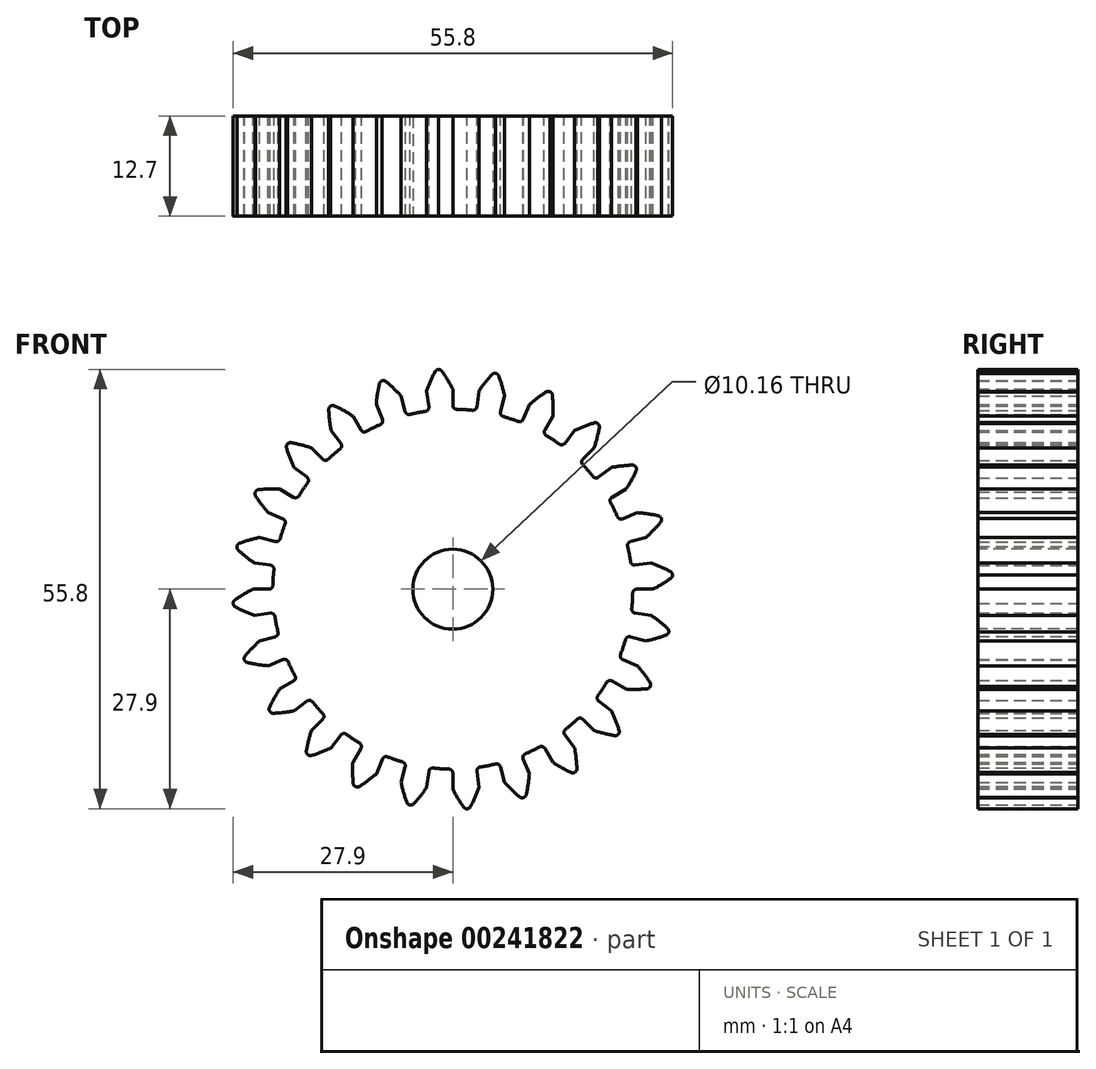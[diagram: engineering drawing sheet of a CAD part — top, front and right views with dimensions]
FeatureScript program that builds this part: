
annotation { "Feature Type Name" : "Feature", "Feature Type Description" : "" }
export const myFeature = defineFeature(function(context is Context, id is Id, definition is map)
    precondition{}
    {
        {
            var Q0;
            Q0=qCreatedBy(makeId("Front.planeOp"),FACE);
            var sketch = newSketch(context, id + "F0", { "sketchPlane" : qUnion([Q0])});
            skArc(sketch, "E0", {"start": v(-3.48, 22.6) * mm, "mid": v(1.5, -22.81) * mm, "end": v(0.5, 22.85) * mm});
            skLineSegment(sketch, "E1", {"start": v(0, 0) * mm, "end": v(-2.26, 34.54) * mm, "construction": true});
            skLineSegment(sketch, "E2", {"start": v(-1.78, 27.9) * mm, "end": v(-1.83, 27.9) * mm});
            skLineSegment(sketch, "E3", {"start": v(0, 25.4) * mm, "end": v(0, 23.36) * mm});
            skArc(sketch, "E4.trimOffspring", {"start": v(0, 25.4) * mm, "mid": v(-0.64, 26.56) * mm, "end": v(-1.37, 27.68) * mm});
            skLineSegment(sketch, "E5.MirrorCS", {"start": v(-1.87, 27.9) * mm, "end": v(-1.83, 27.9) * mm});
            skArc(sketch, "E6.MirrorCS", {"start": v(-3.32, 25.18) * mm, "mid": v(-2.83, 26.42) * mm, "end": v(-2.26, 27.62) * mm});
            skLineSegment(sketch, "E7.MirrorCS", {"start": v(-3.32, 25.18) * mm, "end": v(-3.05, 23.16) * mm});
            skPoint(sketch, "E8.visualSharp", {"position": v(-2.13, 27.86) * mm});
            skArc(sketch, "E8.filletArc", {"start": v(-1.87, 27.9) * mm, "mid": v(-2.1, 27.8) * mm, "end": v(-2.26, 27.62) * mm});
            skPoint(sketch, "E9.visualSharp", {"position": v(-1.52, 27.9) * mm});
            skArc(sketch, "E9.filletArc", {"start": v(-1.37, 27.68) * mm, "mid": v(-1.55, 27.84) * mm, "end": v(-1.78, 27.9) * mm});
            skPoint(sketch, "E10.visualSharp", {"position": v(-2.98, 22.66) * mm});
            skArc(sketch, "E10.filletArc", {"start": v(-3.48, 22.6) * mm, "mid": v(-3.15, 22.8) * mm, "end": v(-3.05, 23.16) * mm});
            skPoint(sketch, "E11.visualSharp", {"position": v(0, 22.86) * mm});
            skArc(sketch, "E11.filletArc", {"start": v(0, 23.36) * mm, "mid": v(0.14, 23) * mm, "end": v(0.5, 22.85) * mm});
            skArc(sketch, "E12.1.0", {"start": v(-9.03, 26.46) * mm, "mid": v(-9.22, 26.31) * mm, "end": v(-9.33, 26.1) * mm});
            skArc(sketch, "E12.1.1", {"start": v(-9.72, 23.47) * mm, "mid": v(-9.57, 24.79) * mm, "end": v(-9.33, 26.1) * mm});
            skLineSegment(sketch, "E12.1.2", {"start": v(-9.72, 23.47) * mm, "end": v(-8.94, 21.58) * mm});
            skArc(sketch, "E12.1.3", {"start": v(-9.2, 20.92) * mm, "mid": v(-8.94, 21.2) * mm, "end": v(-8.94, 21.58) * mm});
            skArc(sketch, "E12.1.4", {"start": v(-6.57, 24.53) * mm, "mid": v(-7.5, 25.5) * mm, "end": v(-8.49, 26.38) * mm});
            skLineSegment(sketch, "E12.1.5", {"start": v(-6.57, 24.53) * mm, "end": v(-6.05, 22.57) * mm});
            skArc(sketch, "E12.1.6", {"start": v(-6.05, 22.57) * mm, "mid": v(-5.81, 22.26) * mm, "end": v(-5.44, 22.2) * mm});
            skArc(sketch, "E12.1.7", {"start": v(-8.49, 26.38) * mm, "mid": v(-8.7, 26.5) * mm, "end": v(-8.94, 26.49) * mm});
            skLineSegment(sketch, "E12.1.8", {"start": v(-8.94, 26.49) * mm, "end": v(-8.99, 26.47) * mm});
            skLineSegment(sketch, "E12.1.9", {"start": v(-9.03, 26.46) * mm, "end": v(-8.99, 26.47) * mm});
            skArc(sketch, "E12.2.0", {"start": v(-15.57, 23.22) * mm, "mid": v(-15.72, 23.03) * mm, "end": v(-15.77, 22.8) * mm});
            skArc(sketch, "E12.2.1", {"start": v(-15.46, 20.15) * mm, "mid": v(-15.66, 21.47) * mm, "end": v(-15.77, 22.8) * mm});
            skLineSegment(sketch, "E12.2.2", {"start": v(-15.46, 20.15) * mm, "end": v(-14.22, 18.53) * mm});
            skArc(sketch, "E12.2.3", {"start": v(-14.3, 17.83) * mm, "mid": v(-14.12, 18.16) * mm, "end": v(-14.22, 18.53) * mm});
            skArc(sketch, "E12.2.4", {"start": v(-12.7, 22) * mm, "mid": v(-13.84, 22.68) * mm, "end": v(-15.03, 23.29) * mm});
            skLineSegment(sketch, "E12.2.5", {"start": v(-12.7, 22) * mm, "end": v(-11.68, 20.23) * mm});
            skArc(sketch, "E12.2.6", {"start": v(-11.68, 20.23) * mm, "mid": v(-11.38, 20) * mm, "end": v(-11, 20.04) * mm});
            skArc(sketch, "E12.2.7", {"start": v(-15.03, 23.29) * mm, "mid": v(-15.26, 23.34) * mm, "end": v(-15.5, 23.27) * mm});
            skLineSegment(sketch, "E12.2.8", {"start": v(-15.5, 23.27) * mm, "end": v(-15.53, 23.25) * mm});
            skLineSegment(sketch, "E12.2.9", {"start": v(-15.57, 23.22) * mm, "end": v(-15.53, 23.25) * mm});
            skArc(sketch, "E12.3.0", {"start": v(-21.05, 18.4) * mm, "mid": v(-21.14, 18.18) * mm, "end": v(-21.13, 17.94) * mm});
            skArc(sketch, "E12.3.1", {"start": v(-20.15, 15.46) * mm, "mid": v(-20.68, 16.68) * mm, "end": v(-21.13, 17.94) * mm});
            skLineSegment(sketch, "E12.3.2", {"start": v(-20.15, 15.46) * mm, "end": v(-18.53, 14.22) * mm});
            skArc(sketch, "E12.3.3", {"start": v(-18.43, 13.52) * mm, "mid": v(-18.34, 13.9) * mm, "end": v(-18.53, 14.22) * mm});
            skArc(sketch, "E12.3.4", {"start": v(-17.96, 17.96) * mm, "mid": v(-19.24, 18.33) * mm, "end": v(-20.54, 18.6) * mm});
            skLineSegment(sketch, "E12.3.5", {"start": v(-17.96, 17.96) * mm, "end": v(-16.52, 16.52) * mm});
            skArc(sketch, "E12.3.6", {"start": v(-16.52, 16.52) * mm, "mid": v(-16.17, 16.37) * mm, "end": v(-15.8, 16.51) * mm});
            skArc(sketch, "E12.3.7", {"start": v(-20.54, 18.6) * mm, "mid": v(-20.78, 18.6) * mm, "end": v(-20.99, 18.47) * mm});
            skLineSegment(sketch, "E12.3.8", {"start": v(-20.99, 18.47) * mm, "end": v(-21.02, 18.43) * mm});
            skLineSegment(sketch, "E12.3.9", {"start": v(-21.05, 18.4) * mm, "end": v(-21.02, 18.43) * mm});
            skArc(sketch, "E12.4.0", {"start": v(-25.1, 12.32) * mm, "mid": v(-25.13, 12.09) * mm, "end": v(-25.05, 11.86) * mm});
            skArc(sketch, "E12.4.1", {"start": v(-23.47, 9.72) * mm, "mid": v(-24.3, 10.76) * mm, "end": v(-25.05, 11.86) * mm});
            skLineSegment(sketch, "E12.4.2", {"start": v(-23.47, 9.72) * mm, "end": v(-21.58, 8.94) * mm});
            skArc(sketch, "E12.4.3", {"start": v(-21.3, 8.29) * mm, "mid": v(-21.31, 8.67) * mm, "end": v(-21.58, 8.94) * mm});
            skArc(sketch, "E12.4.4", {"start": v(-22, 12.7) * mm, "mid": v(-23.33, 12.72) * mm, "end": v(-24.66, 12.66) * mm});
            skLineSegment(sketch, "E12.4.5", {"start": v(-22, 12.7) * mm, "end": v(-20.23, 11.68) * mm});
            skArc(sketch, "E12.4.6", {"start": v(-20.23, 11.68) * mm, "mid": v(-19.85, 11.63) * mm, "end": v(-19.54, 11.86) * mm});
            skArc(sketch, "E12.4.7", {"start": v(-24.66, 12.66) * mm, "mid": v(-24.89, 12.58) * mm, "end": v(-25.05, 12.4) * mm});
            skLineSegment(sketch, "E12.4.8", {"start": v(-25.05, 12.4) * mm, "end": v(-25.08, 12.37) * mm});
            skLineSegment(sketch, "E12.4.9", {"start": v(-25.1, 12.32) * mm, "end": v(-25.08, 12.37) * mm});
            skArc(sketch, "E12.5.0", {"start": v(-27.43, 5.41) * mm, "mid": v(-27.4, 5.17) * mm, "end": v(-27.27, 4.97) * mm});
            skArc(sketch, "E12.5.1", {"start": v(-25.18, 3.32) * mm, "mid": v(-26.25, 4.1) * mm, "end": v(-27.27, 4.97) * mm});
            skLineSegment(sketch, "E12.5.2", {"start": v(-25.18, 3.32) * mm, "end": v(-23.16, 3.05) * mm});
            skArc(sketch, "E12.5.3", {"start": v(-22.72, 2.5) * mm, "mid": v(-22.83, 2.86) * mm, "end": v(-23.16, 3.05) * mm});
            skArc(sketch, "E12.5.4", {"start": v(-24.53, 6.57) * mm, "mid": v(-25.83, 6.25) * mm, "end": v(-27.1, 5.84) * mm});
            skLineSegment(sketch, "E12.5.5", {"start": v(-24.53, 6.57) * mm, "end": v(-22.57, 6.05) * mm});
            skArc(sketch, "E12.5.6", {"start": v(-22.57, 6.05) * mm, "mid": v(-22.19, 6.1) * mm, "end": v(-21.95, 6.4) * mm});
            skArc(sketch, "E12.5.7", {"start": v(-27.1, 5.84) * mm, "mid": v(-27.3, 5.7) * mm, "end": v(-27.4, 5.5) * mm});
            skLineSegment(sketch, "E12.5.8", {"start": v(-27.4, 5.5) * mm, "end": v(-27.42, 5.45) * mm});
            skLineSegment(sketch, "E12.5.9", {"start": v(-27.43, 5.41) * mm, "end": v(-27.42, 5.45) * mm});
            skArc(sketch, "E12.6.0", {"start": v(-27.9, -1.87) * mm, "mid": v(-27.8, -2.1) * mm, "end": v(-27.62, -2.26) * mm});
            skArc(sketch, "E12.6.1", {"start": v(-25.18, -3.32) * mm, "mid": v(-26.42, -2.83) * mm, "end": v(-27.62, -2.26) * mm});
            skLineSegment(sketch, "E12.6.2", {"start": v(-25.18, -3.32) * mm, "end": v(-23.16, -3.05) * mm});
            skArc(sketch, "E12.6.3", {"start": v(-22.6, -3.48) * mm, "mid": v(-22.8, -3.15) * mm, "end": v(-23.16, -3.05) * mm});
            skArc(sketch, "E12.6.4", {"start": v(-25.4, 0) * mm, "mid": v(-26.56, -0.64) * mm, "end": v(-27.68, -1.37) * mm});
            skLineSegment(sketch, "E12.6.5", {"start": v(-25.4, 0) * mm, "end": v(-23.36, 0) * mm});
            skArc(sketch, "E12.6.6", {"start": v(-23.36, 0) * mm, "mid": v(-23, 0.14) * mm, "end": v(-22.85, 0.5) * mm});
            skArc(sketch, "E12.6.7", {"start": v(-27.68, -1.37) * mm, "mid": v(-27.84, -1.55) * mm, "end": v(-27.9, -1.78) * mm});
            skLineSegment(sketch, "E12.6.8", {"start": v(-27.9, -1.78) * mm, "end": v(-27.9, -1.83) * mm});
            skLineSegment(sketch, "E12.6.9", {"start": v(-27.9, -1.87) * mm, "end": v(-27.9, -1.83) * mm});
            skArc(sketch, "E12.7.0", {"start": v(-26.46, -9.03) * mm, "mid": v(-26.31, -9.22) * mm, "end": v(-26.1, -9.33) * mm});
            skArc(sketch, "E12.7.1", {"start": v(-23.47, -9.72) * mm, "mid": v(-24.79, -9.57) * mm, "end": v(-26.1, -9.33) * mm});
            skLineSegment(sketch, "E12.7.2", {"start": v(-23.47, -9.72) * mm, "end": v(-21.58, -8.94) * mm});
            skArc(sketch, "E12.7.3", {"start": v(-20.92, -9.2) * mm, "mid": v(-21.2, -8.94) * mm, "end": v(-21.58, -8.94) * mm});
            skArc(sketch, "E12.7.4", {"start": v(-24.53, -6.57) * mm, "mid": v(-25.5, -7.5) * mm, "end": v(-26.38, -8.49) * mm});
            skLineSegment(sketch, "E12.7.5", {"start": v(-24.53, -6.57) * mm, "end": v(-22.57, -6.05) * mm});
            skArc(sketch, "E12.7.6", {"start": v(-22.57, -6.05) * mm, "mid": v(-22.26, -5.81) * mm, "end": v(-22.2, -5.44) * mm});
            skArc(sketch, "E12.7.7", {"start": v(-26.38, -8.49) * mm, "mid": v(-26.5, -8.7) * mm, "end": v(-26.49, -8.94) * mm});
            skLineSegment(sketch, "E12.7.8", {"start": v(-26.49, -8.94) * mm, "end": v(-26.47, -8.99) * mm});
            skLineSegment(sketch, "E12.7.9", {"start": v(-26.46, -9.03) * mm, "end": v(-26.47, -8.99) * mm});
            skArc(sketch, "E12.8.0", {"start": v(-23.22, -15.57) * mm, "mid": v(-23.03, -15.72) * mm, "end": v(-22.8, -15.77) * mm});
            skArc(sketch, "E12.8.1", {"start": v(-20.15, -15.46) * mm, "mid": v(-21.47, -15.66) * mm, "end": v(-22.8, -15.77) * mm});
            skLineSegment(sketch, "E12.8.2", {"start": v(-20.15, -15.46) * mm, "end": v(-18.53, -14.22) * mm});
            skArc(sketch, "E12.8.3", {"start": v(-17.83, -14.3) * mm, "mid": v(-18.16, -14.12) * mm, "end": v(-18.53, -14.22) * mm});
            skArc(sketch, "E12.8.4", {"start": v(-22, -12.7) * mm, "mid": v(-22.68, -13.84) * mm, "end": v(-23.29, -15.03) * mm});
            skLineSegment(sketch, "E12.8.5", {"start": v(-22, -12.7) * mm, "end": v(-20.23, -11.68) * mm});
            skArc(sketch, "E12.8.6", {"start": v(-20.23, -11.68) * mm, "mid": v(-20, -11.38) * mm, "end": v(-20.04, -11) * mm});
            skArc(sketch, "E12.8.7", {"start": v(-23.29, -15.03) * mm, "mid": v(-23.34, -15.26) * mm, "end": v(-23.27, -15.5) * mm});
            skLineSegment(sketch, "E12.8.8", {"start": v(-23.27, -15.5) * mm, "end": v(-23.25, -15.53) * mm});
            skLineSegment(sketch, "E12.8.9", {"start": v(-23.22, -15.57) * mm, "end": v(-23.25, -15.53) * mm});
            skArc(sketch, "E12.9.0", {"start": v(-18.4, -21.05) * mm, "mid": v(-18.18, -21.14) * mm, "end": v(-17.94, -21.13) * mm});
            skArc(sketch, "E12.9.1", {"start": v(-15.46, -20.15) * mm, "mid": v(-16.68, -20.68) * mm, "end": v(-17.94, -21.13) * mm});
            skLineSegment(sketch, "E12.9.2", {"start": v(-15.46, -20.15) * mm, "end": v(-14.22, -18.53) * mm});
            skArc(sketch, "E12.9.3", {"start": v(-13.52, -18.43) * mm, "mid": v(-13.9, -18.34) * mm, "end": v(-14.22, -18.53) * mm});
            skArc(sketch, "E12.9.4", {"start": v(-17.96, -17.96) * mm, "mid": v(-18.33, -19.24) * mm, "end": v(-18.6, -20.54) * mm});
            skLineSegment(sketch, "E12.9.5", {"start": v(-17.96, -17.96) * mm, "end": v(-16.52, -16.52) * mm});
            skArc(sketch, "E12.9.6", {"start": v(-16.52, -16.52) * mm, "mid": v(-16.37, -16.17) * mm, "end": v(-16.51, -15.8) * mm});
            skArc(sketch, "E12.9.7", {"start": v(-18.6, -20.54) * mm, "mid": v(-18.6, -20.78) * mm, "end": v(-18.47, -20.99) * mm});
            skLineSegment(sketch, "E12.9.8", {"start": v(-18.47, -20.99) * mm, "end": v(-18.43, -21.02) * mm});
            skLineSegment(sketch, "E12.9.9", {"start": v(-18.4, -21.05) * mm, "end": v(-18.43, -21.02) * mm});
            skArc(sketch, "E12.10.0", {"start": v(-12.32, -25.1) * mm, "mid": v(-12.09, -25.13) * mm, "end": v(-11.86, -25.05) * mm});
            skArc(sketch, "E12.10.1", {"start": v(-9.72, -23.47) * mm, "mid": v(-10.76, -24.3) * mm, "end": v(-11.86, -25.05) * mm});
            skLineSegment(sketch, "E12.10.2", {"start": v(-9.72, -23.47) * mm, "end": v(-8.94, -21.58) * mm});
            skArc(sketch, "E12.10.3", {"start": v(-8.29, -21.3) * mm, "mid": v(-8.67, -21.31) * mm, "end": v(-8.94, -21.58) * mm});
            skArc(sketch, "E12.10.4", {"start": v(-12.7, -22) * mm, "mid": v(-12.72, -23.33) * mm, "end": v(-12.66, -24.66) * mm});
            skLineSegment(sketch, "E12.10.5", {"start": v(-12.7, -22) * mm, "end": v(-11.68, -20.23) * mm});
            skArc(sketch, "E12.10.6", {"start": v(-11.68, -20.23) * mm, "mid": v(-11.63, -19.85) * mm, "end": v(-11.86, -19.54) * mm});
            skArc(sketch, "E12.10.7", {"start": v(-12.66, -24.66) * mm, "mid": v(-12.58, -24.89) * mm, "end": v(-12.4, -25.05) * mm});
            skLineSegment(sketch, "E12.10.8", {"start": v(-12.4, -25.05) * mm, "end": v(-12.37, -25.08) * mm});
            skLineSegment(sketch, "E12.10.9", {"start": v(-12.32, -25.1) * mm, "end": v(-12.37, -25.08) * mm});
            skArc(sketch, "E12.11.0", {"start": v(-5.41, -27.43) * mm, "mid": v(-5.17, -27.4) * mm, "end": v(-4.97, -27.27) * mm});
            skArc(sketch, "E12.11.1", {"start": v(-3.32, -25.18) * mm, "mid": v(-4.1, -26.25) * mm, "end": v(-4.97, -27.27) * mm});
            skLineSegment(sketch, "E12.11.2", {"start": v(-3.32, -25.18) * mm, "end": v(-3.05, -23.16) * mm});
            skArc(sketch, "E12.11.3", {"start": v(-2.5, -22.72) * mm, "mid": v(-2.86, -22.83) * mm, "end": v(-3.05, -23.16) * mm});
            skArc(sketch, "E12.11.4", {"start": v(-6.57, -24.53) * mm, "mid": v(-6.25, -25.83) * mm, "end": v(-5.84, -27.1) * mm});
            skLineSegment(sketch, "E12.11.5", {"start": v(-6.57, -24.53) * mm, "end": v(-6.05, -22.57) * mm});
            skArc(sketch, "E12.11.6", {"start": v(-6.05, -22.57) * mm, "mid": v(-6.1, -22.19) * mm, "end": v(-6.4, -21.95) * mm});
            skArc(sketch, "E12.11.7", {"start": v(-5.84, -27.1) * mm, "mid": v(-5.7, -27.3) * mm, "end": v(-5.5, -27.4) * mm});
            skLineSegment(sketch, "E12.11.8", {"start": v(-5.5, -27.4) * mm, "end": v(-5.45, -27.42) * mm});
            skLineSegment(sketch, "E12.11.9", {"start": v(-5.41, -27.43) * mm, "end": v(-5.45, -27.42) * mm});
            skArc(sketch, "E12.12.0", {"start": v(1.87, -27.9) * mm, "mid": v(2.1, -27.8) * mm, "end": v(2.26, -27.62) * mm});
            skArc(sketch, "E12.12.1", {"start": v(3.32, -25.18) * mm, "mid": v(2.83, -26.42) * mm, "end": v(2.26, -27.62) * mm});
            skLineSegment(sketch, "E12.12.2", {"start": v(3.32, -25.18) * mm, "end": v(3.05, -23.16) * mm});
            skArc(sketch, "E12.12.3", {"start": v(3.48, -22.6) * mm, "mid": v(3.15, -22.8) * mm, "end": v(3.05, -23.16) * mm});
            skArc(sketch, "E12.12.4", {"start": v(0, -25.4) * mm, "mid": v(0.64, -26.56) * mm, "end": v(1.37, -27.68) * mm});
            skLineSegment(sketch, "E12.12.5", {"start": v(0, -25.4) * mm, "end": v(0, -23.36) * mm});
            skArc(sketch, "E12.12.6", {"start": v(0, -23.36) * mm, "mid": v(-0.14, -23) * mm, "end": v(-0.5, -22.85) * mm});
            skArc(sketch, "E12.12.7", {"start": v(1.37, -27.68) * mm, "mid": v(1.55, -27.84) * mm, "end": v(1.78, -27.9) * mm});
            skLineSegment(sketch, "E12.12.8", {"start": v(1.78, -27.9) * mm, "end": v(1.83, -27.9) * mm});
            skLineSegment(sketch, "E12.12.9", {"start": v(1.87, -27.9) * mm, "end": v(1.83, -27.9) * mm});
            skArc(sketch, "E12.13.0", {"start": v(9.03, -26.46) * mm, "mid": v(9.22, -26.31) * mm, "end": v(9.33, -26.1) * mm});
            skArc(sketch, "E12.13.1", {"start": v(9.72, -23.47) * mm, "mid": v(9.57, -24.79) * mm, "end": v(9.33, -26.1) * mm});
            skLineSegment(sketch, "E12.13.2", {"start": v(9.72, -23.47) * mm, "end": v(8.94, -21.58) * mm});
            skArc(sketch, "E12.13.3", {"start": v(9.2, -20.92) * mm, "mid": v(8.94, -21.2) * mm, "end": v(8.94, -21.58) * mm});
            skArc(sketch, "E12.13.4", {"start": v(6.57, -24.53) * mm, "mid": v(7.5, -25.5) * mm, "end": v(8.49, -26.38) * mm});
            skLineSegment(sketch, "E12.13.5", {"start": v(6.57, -24.53) * mm, "end": v(6.05, -22.57) * mm});
            skArc(sketch, "E12.13.6", {"start": v(6.05, -22.57) * mm, "mid": v(5.81, -22.26) * mm, "end": v(5.44, -22.2) * mm});
            skArc(sketch, "E12.13.7", {"start": v(8.49, -26.38) * mm, "mid": v(8.7, -26.5) * mm, "end": v(8.94, -26.49) * mm});
            skLineSegment(sketch, "E12.13.8", {"start": v(8.94, -26.49) * mm, "end": v(8.99, -26.47) * mm});
            skLineSegment(sketch, "E12.13.9", {"start": v(9.03, -26.46) * mm, "end": v(8.99, -26.47) * mm});
            skArc(sketch, "E12.14.0", {"start": v(15.57, -23.22) * mm, "mid": v(15.72, -23.03) * mm, "end": v(15.77, -22.8) * mm});
            skArc(sketch, "E12.14.1", {"start": v(15.46, -20.15) * mm, "mid": v(15.66, -21.47) * mm, "end": v(15.77, -22.8) * mm});
            skLineSegment(sketch, "E12.14.2", {"start": v(15.46, -20.15) * mm, "end": v(14.22, -18.53) * mm});
            skArc(sketch, "E12.14.3", {"start": v(14.3, -17.83) * mm, "mid": v(14.12, -18.16) * mm, "end": v(14.22, -18.53) * mm});
            skArc(sketch, "E12.14.4", {"start": v(12.7, -22) * mm, "mid": v(13.84, -22.68) * mm, "end": v(15.03, -23.29) * mm});
            skLineSegment(sketch, "E12.14.5", {"start": v(12.7, -22) * mm, "end": v(11.68, -20.23) * mm});
            skArc(sketch, "E12.14.6", {"start": v(11.68, -20.23) * mm, "mid": v(11.38, -20) * mm, "end": v(11, -20.04) * mm});
            skArc(sketch, "E12.14.7", {"start": v(15.03, -23.29) * mm, "mid": v(15.26, -23.34) * mm, "end": v(15.5, -23.27) * mm});
            skLineSegment(sketch, "E12.14.8", {"start": v(15.5, -23.27) * mm, "end": v(15.53, -23.25) * mm});
            skLineSegment(sketch, "E12.14.9", {"start": v(15.57, -23.22) * mm, "end": v(15.53, -23.25) * mm});
            skArc(sketch, "E12.15.0", {"start": v(21.05, -18.4) * mm, "mid": v(21.14, -18.18) * mm, "end": v(21.13, -17.94) * mm});
            skArc(sketch, "E12.15.1", {"start": v(20.15, -15.46) * mm, "mid": v(20.68, -16.68) * mm, "end": v(21.13, -17.94) * mm});
            skLineSegment(sketch, "E12.15.2", {"start": v(20.15, -15.46) * mm, "end": v(18.53, -14.22) * mm});
            skArc(sketch, "E12.15.3", {"start": v(18.43, -13.52) * mm, "mid": v(18.34, -13.9) * mm, "end": v(18.53, -14.22) * mm});
            skArc(sketch, "E12.15.4", {"start": v(17.96, -17.96) * mm, "mid": v(19.24, -18.33) * mm, "end": v(20.54, -18.6) * mm});
            skLineSegment(sketch, "E12.15.5", {"start": v(17.96, -17.96) * mm, "end": v(16.52, -16.52) * mm});
            skArc(sketch, "E12.15.6", {"start": v(16.52, -16.52) * mm, "mid": v(16.17, -16.37) * mm, "end": v(15.8, -16.51) * mm});
            skArc(sketch, "E12.15.7", {"start": v(20.54, -18.6) * mm, "mid": v(20.78, -18.6) * mm, "end": v(20.99, -18.47) * mm});
            skLineSegment(sketch, "E12.15.8", {"start": v(20.99, -18.47) * mm, "end": v(21.02, -18.43) * mm});
            skLineSegment(sketch, "E12.15.9", {"start": v(21.05, -18.4) * mm, "end": v(21.02, -18.43) * mm});
            skArc(sketch, "E12.16.0", {"start": v(25.1, -12.32) * mm, "mid": v(25.13, -12.09) * mm, "end": v(25.05, -11.86) * mm});
            skArc(sketch, "E12.16.1", {"start": v(23.47, -9.72) * mm, "mid": v(24.3, -10.76) * mm, "end": v(25.05, -11.86) * mm});
            skLineSegment(sketch, "E12.16.2", {"start": v(23.47, -9.72) * mm, "end": v(21.58, -8.94) * mm});
            skArc(sketch, "E12.16.3", {"start": v(21.3, -8.29) * mm, "mid": v(21.31, -8.67) * mm, "end": v(21.58, -8.94) * mm});
            skArc(sketch, "E12.16.4", {"start": v(22, -12.7) * mm, "mid": v(23.33, -12.72) * mm, "end": v(24.66, -12.66) * mm});
            skLineSegment(sketch, "E12.16.5", {"start": v(22, -12.7) * mm, "end": v(20.23, -11.68) * mm});
            skArc(sketch, "E12.16.6", {"start": v(20.23, -11.68) * mm, "mid": v(19.85, -11.63) * mm, "end": v(19.54, -11.86) * mm});
            skArc(sketch, "E12.16.7", {"start": v(24.66, -12.66) * mm, "mid": v(24.89, -12.58) * mm, "end": v(25.05, -12.4) * mm});
            skLineSegment(sketch, "E12.16.8", {"start": v(25.05, -12.4) * mm, "end": v(25.08, -12.37) * mm});
            skLineSegment(sketch, "E12.16.9", {"start": v(25.1, -12.32) * mm, "end": v(25.08, -12.37) * mm});
            skArc(sketch, "E12.17.0", {"start": v(27.43, -5.41) * mm, "mid": v(27.4, -5.17) * mm, "end": v(27.27, -4.97) * mm});
            skArc(sketch, "E12.17.1", {"start": v(25.18, -3.32) * mm, "mid": v(26.25, -4.1) * mm, "end": v(27.27, -4.97) * mm});
            skLineSegment(sketch, "E12.17.2", {"start": v(25.18, -3.32) * mm, "end": v(23.16, -3.05) * mm});
            skArc(sketch, "E12.17.3", {"start": v(22.72, -2.5) * mm, "mid": v(22.83, -2.86) * mm, "end": v(23.16, -3.05) * mm});
            skArc(sketch, "E12.17.4", {"start": v(24.53, -6.57) * mm, "mid": v(25.83, -6.25) * mm, "end": v(27.1, -5.84) * mm});
            skLineSegment(sketch, "E12.17.5", {"start": v(24.53, -6.57) * mm, "end": v(22.57, -6.05) * mm});
            skArc(sketch, "E12.17.6", {"start": v(22.57, -6.05) * mm, "mid": v(22.19, -6.1) * mm, "end": v(21.95, -6.4) * mm});
            skArc(sketch, "E12.17.7", {"start": v(27.1, -5.84) * mm, "mid": v(27.3, -5.7) * mm, "end": v(27.4, -5.5) * mm});
            skLineSegment(sketch, "E12.17.8", {"start": v(27.4, -5.5) * mm, "end": v(27.42, -5.45) * mm});
            skLineSegment(sketch, "E12.17.9", {"start": v(27.43, -5.41) * mm, "end": v(27.42, -5.45) * mm});
            skArc(sketch, "E12.18.0", {"start": v(27.9, 1.87) * mm, "mid": v(27.8, 2.1) * mm, "end": v(27.62, 2.26) * mm});
            skArc(sketch, "E12.18.1", {"start": v(25.18, 3.32) * mm, "mid": v(26.42, 2.83) * mm, "end": v(27.62, 2.26) * mm});
            skLineSegment(sketch, "E12.18.2", {"start": v(25.18, 3.32) * mm, "end": v(23.16, 3.05) * mm});
            skArc(sketch, "E12.18.3", {"start": v(22.6, 3.48) * mm, "mid": v(22.8, 3.15) * mm, "end": v(23.16, 3.05) * mm});
            skArc(sketch, "E12.18.4", {"start": v(25.4, 0) * mm, "mid": v(26.56, 0.64) * mm, "end": v(27.68, 1.37) * mm});
            skLineSegment(sketch, "E12.18.5", {"start": v(25.4, 0) * mm, "end": v(23.36, 0) * mm});
            skArc(sketch, "E12.18.6", {"start": v(23.36, 0) * mm, "mid": v(23, -0.14) * mm, "end": v(22.85, -0.5) * mm});
            skArc(sketch, "E12.18.7", {"start": v(27.68, 1.37) * mm, "mid": v(27.84, 1.55) * mm, "end": v(27.9, 1.78) * mm});
            skLineSegment(sketch, "E12.18.8", {"start": v(27.9, 1.78) * mm, "end": v(27.9, 1.83) * mm});
            skLineSegment(sketch, "E12.18.9", {"start": v(27.9, 1.87) * mm, "end": v(27.9, 1.83) * mm});
            skArc(sketch, "E12.19.0", {"start": v(26.46, 9.03) * mm, "mid": v(26.31, 9.22) * mm, "end": v(26.1, 9.33) * mm});
            skArc(sketch, "E12.19.1", {"start": v(23.47, 9.72) * mm, "mid": v(24.79, 9.57) * mm, "end": v(26.1, 9.33) * mm});
            skLineSegment(sketch, "E12.19.2", {"start": v(23.47, 9.72) * mm, "end": v(21.58, 8.94) * mm});
            skArc(sketch, "E12.19.3", {"start": v(20.92, 9.2) * mm, "mid": v(21.2, 8.94) * mm, "end": v(21.58, 8.94) * mm});
            skArc(sketch, "E12.19.4", {"start": v(24.53, 6.57) * mm, "mid": v(25.5, 7.5) * mm, "end": v(26.38, 8.49) * mm});
            skLineSegment(sketch, "E12.19.5", {"start": v(24.53, 6.57) * mm, "end": v(22.57, 6.05) * mm});
            skArc(sketch, "E12.19.6", {"start": v(22.57, 6.05) * mm, "mid": v(22.26, 5.81) * mm, "end": v(22.2, 5.44) * mm});
            skArc(sketch, "E12.19.7", {"start": v(26.38, 8.49) * mm, "mid": v(26.5, 8.7) * mm, "end": v(26.49, 8.94) * mm});
            skLineSegment(sketch, "E12.19.8", {"start": v(26.49, 8.94) * mm, "end": v(26.47, 8.99) * mm});
            skLineSegment(sketch, "E12.19.9", {"start": v(26.46, 9.03) * mm, "end": v(26.47, 8.99) * mm});
            skArc(sketch, "E12.20.0", {"start": v(23.22, 15.57) * mm, "mid": v(23.03, 15.72) * mm, "end": v(22.8, 15.77) * mm});
            skArc(sketch, "E12.20.1", {"start": v(20.15, 15.46) * mm, "mid": v(21.47, 15.66) * mm, "end": v(22.8, 15.77) * mm});
            skLineSegment(sketch, "E12.20.2", {"start": v(20.15, 15.46) * mm, "end": v(18.53, 14.22) * mm});
            skArc(sketch, "E12.20.3", {"start": v(17.83, 14.3) * mm, "mid": v(18.16, 14.12) * mm, "end": v(18.53, 14.22) * mm});
            skArc(sketch, "E12.20.4", {"start": v(22, 12.7) * mm, "mid": v(22.68, 13.84) * mm, "end": v(23.29, 15.03) * mm});
            skLineSegment(sketch, "E12.20.5", {"start": v(22, 12.7) * mm, "end": v(20.23, 11.68) * mm});
            skArc(sketch, "E12.20.6", {"start": v(20.23, 11.68) * mm, "mid": v(20, 11.38) * mm, "end": v(20.04, 11) * mm});
            skArc(sketch, "E12.20.7", {"start": v(23.29, 15.03) * mm, "mid": v(23.34, 15.26) * mm, "end": v(23.27, 15.5) * mm});
            skLineSegment(sketch, "E12.20.8", {"start": v(23.27, 15.5) * mm, "end": v(23.25, 15.53) * mm});
            skLineSegment(sketch, "E12.20.9", {"start": v(23.22, 15.57) * mm, "end": v(23.25, 15.53) * mm});
            skArc(sketch, "E12.21.0", {"start": v(18.4, 21.05) * mm, "mid": v(18.18, 21.14) * mm, "end": v(17.94, 21.13) * mm});
            skArc(sketch, "E12.21.1", {"start": v(15.46, 20.15) * mm, "mid": v(16.68, 20.68) * mm, "end": v(17.94, 21.13) * mm});
            skLineSegment(sketch, "E12.21.2", {"start": v(15.46, 20.15) * mm, "end": v(14.22, 18.53) * mm});
            skArc(sketch, "E12.21.3", {"start": v(13.52, 18.43) * mm, "mid": v(13.9, 18.34) * mm, "end": v(14.22, 18.53) * mm});
            skArc(sketch, "E12.21.4", {"start": v(17.96, 17.96) * mm, "mid": v(18.33, 19.24) * mm, "end": v(18.6, 20.54) * mm});
            skLineSegment(sketch, "E12.21.5", {"start": v(17.96, 17.96) * mm, "end": v(16.52, 16.52) * mm});
            skArc(sketch, "E12.21.6", {"start": v(16.52, 16.52) * mm, "mid": v(16.37, 16.17) * mm, "end": v(16.51, 15.8) * mm});
            skArc(sketch, "E12.21.7", {"start": v(18.6, 20.54) * mm, "mid": v(18.6, 20.78) * mm, "end": v(18.47, 20.99) * mm});
            skLineSegment(sketch, "E12.21.8", {"start": v(18.47, 20.99) * mm, "end": v(18.43, 21.02) * mm});
            skLineSegment(sketch, "E12.21.9", {"start": v(18.4, 21.05) * mm, "end": v(18.43, 21.02) * mm});
            skArc(sketch, "E12.22.0", {"start": v(12.32, 25.1) * mm, "mid": v(12.09, 25.13) * mm, "end": v(11.86, 25.05) * mm});
            skArc(sketch, "E12.22.1", {"start": v(9.72, 23.47) * mm, "mid": v(10.76, 24.3) * mm, "end": v(11.86, 25.05) * mm});
            skLineSegment(sketch, "E12.22.2", {"start": v(9.72, 23.47) * mm, "end": v(8.94, 21.58) * mm});
            skArc(sketch, "E12.22.3", {"start": v(8.29, 21.3) * mm, "mid": v(8.67, 21.31) * mm, "end": v(8.94, 21.58) * mm});
            skArc(sketch, "E12.22.4", {"start": v(12.7, 22) * mm, "mid": v(12.72, 23.33) * mm, "end": v(12.66, 24.66) * mm});
            skLineSegment(sketch, "E12.22.5", {"start": v(12.7, 22) * mm, "end": v(11.68, 20.23) * mm});
            skArc(sketch, "E12.22.6", {"start": v(11.68, 20.23) * mm, "mid": v(11.63, 19.85) * mm, "end": v(11.86, 19.54) * mm});
            skArc(sketch, "E12.22.7", {"start": v(12.66, 24.66) * mm, "mid": v(12.58, 24.89) * mm, "end": v(12.4, 25.05) * mm});
            skLineSegment(sketch, "E12.22.8", {"start": v(12.4, 25.05) * mm, "end": v(12.37, 25.08) * mm});
            skLineSegment(sketch, "E12.22.9", {"start": v(12.32, 25.1) * mm, "end": v(12.37, 25.08) * mm});
            skArc(sketch, "E12.23.0", {"start": v(5.41, 27.43) * mm, "mid": v(5.17, 27.4) * mm, "end": v(4.97, 27.27) * mm});
            skArc(sketch, "E12.23.1", {"start": v(3.32, 25.18) * mm, "mid": v(4.1, 26.25) * mm, "end": v(4.97, 27.27) * mm});
            skLineSegment(sketch, "E12.23.2", {"start": v(3.32, 25.18) * mm, "end": v(3.05, 23.16) * mm});
            skArc(sketch, "E12.23.3", {"start": v(2.5, 22.72) * mm, "mid": v(2.86, 22.83) * mm, "end": v(3.05, 23.16) * mm});
            skArc(sketch, "E12.23.4", {"start": v(6.57, 24.53) * mm, "mid": v(6.25, 25.83) * mm, "end": v(5.84, 27.1) * mm});
            skLineSegment(sketch, "E12.23.5", {"start": v(6.57, 24.53) * mm, "end": v(6.05, 22.57) * mm});
            skArc(sketch, "E12.23.6", {"start": v(6.05, 22.57) * mm, "mid": v(6.1, 22.19) * mm, "end": v(6.4, 21.95) * mm});
            skArc(sketch, "E12.23.7", {"start": v(5.84, 27.1) * mm, "mid": v(5.7, 27.3) * mm, "end": v(5.5, 27.4) * mm});
            skLineSegment(sketch, "E12.23.8", {"start": v(5.5, 27.4) * mm, "end": v(5.45, 27.42) * mm});
            skLineSegment(sketch, "E12.23.9", {"start": v(5.41, 27.43) * mm, "end": v(5.45, 27.42) * mm});
            skSolve(sketch);
        }
        {
            var Q0;
            Q0 = qSketchRegion(id + "F0", true);
            extrude(context, id + "F1", {"entities" : qUnion([Q0]), "depth" : 12.7 * mm});
        }
        {
            var Q0;
            Q0=makeQuery(id+"F1.opExtrude","CAP_FACE",FACE,{"disambiguationData":[OSD([sQuery(id+"F0.wireOp",EDGE,"E0"),sQuery(id+"F0.wireOp",EDGE,"E2"),sQuery(id+"F0.wireOp",EDGE,"E3"),sQuery(id+"F0.wireOp",EDGE,"E4.trimOffspring"),sQuery(id+"F0.wireOp",EDGE,"E5.MirrorCS"),sQuery(id+"F0.wireOp",EDGE,"E6.MirrorCS"),sQuery(id+"F0.wireOp",EDGE,"E7.MirrorCS"),sQuery(id+"F0.wireOp",EDGE,"E8.filletArc"),sQuery(id+"F0.wireOp",EDGE,"E9.filletArc"),sQuery(id+"F0.wireOp",EDGE,"E10.filletArc"),sQuery(id+"F0.wireOp",EDGE,"E11.filletArc"),sQuery(id+"F0.wireOp",EDGE,"E12.1.0"),sQuery(id+"F0.wireOp",EDGE,"E12.1.1"),sQuery(id+"F0.wireOp",EDGE,"E12.1.2"),sQuery(id+"F0.wireOp",EDGE,"E12.1.3"),sQuery(id+"F0.wireOp",EDGE,"E12.1.4"),sQuery(id+"F0.wireOp",EDGE,"E12.1.5"),sQuery(id+"F0.wireOp",EDGE,"E12.1.6"),sQuery(id+"F0.wireOp",EDGE,"E12.1.7"),sQuery(id+"F0.wireOp",EDGE,"E12.1.8"),sQuery(id+"F0.wireOp",EDGE,"E12.1.9"),sQuery(id+"F0.wireOp",EDGE,"E12.2.0"),sQuery(id+"F0.wireOp",EDGE,"E12.2.1"),sQuery(id+"F0.wireOp",EDGE,"E12.2.2"),sQuery(id+"F0.wireOp",EDGE,"E12.2.3"),sQuery(id+"F0.wireOp",EDGE,"E12.2.4"),sQuery(id+"F0.wireOp",EDGE,"E12.2.5"),sQuery(id+"F0.wireOp",EDGE,"E12.2.6"),sQuery(id+"F0.wireOp",EDGE,"E12.2.7"),sQuery(id+"F0.wireOp",EDGE,"E12.2.8"),sQuery(id+"F0.wireOp",EDGE,"E12.2.9"),sQuery(id+"F0.wireOp",EDGE,"E12.3.0"),sQuery(id+"F0.wireOp",EDGE,"E12.3.1"),sQuery(id+"F0.wireOp",EDGE,"E12.3.2"),sQuery(id+"F0.wireOp",EDGE,"E12.3.3"),sQuery(id+"F0.wireOp",EDGE,"E12.3.4"),sQuery(id+"F0.wireOp",EDGE,"E12.3.5"),sQuery(id+"F0.wireOp",EDGE,"E12.3.6"),sQuery(id+"F0.wireOp",EDGE,"E12.3.7"),sQuery(id+"F0.wireOp",EDGE,"E12.3.8"),sQuery(id+"F0.wireOp",EDGE,"E12.3.9"),sQuery(id+"F0.wireOp",EDGE,"E12.4.0"),sQuery(id+"F0.wireOp",EDGE,"E12.4.1"),sQuery(id+"F0.wireOp",EDGE,"E12.4.2"),sQuery(id+"F0.wireOp",EDGE,"E12.4.3"),sQuery(id+"F0.wireOp",EDGE,"E12.4.4"),sQuery(id+"F0.wireOp",EDGE,"E12.4.5"),sQuery(id+"F0.wireOp",EDGE,"E12.4.6"),sQuery(id+"F0.wireOp",EDGE,"E12.4.7"),sQuery(id+"F0.wireOp",EDGE,"E12.4.8"),sQuery(id+"F0.wireOp",EDGE,"E12.4.9"),sQuery(id+"F0.wireOp",EDGE,"E12.5.0"),sQuery(id+"F0.wireOp",EDGE,"E12.5.1"),sQuery(id+"F0.wireOp",EDGE,"E12.5.2"),sQuery(id+"F0.wireOp",EDGE,"E12.5.3"),sQuery(id+"F0.wireOp",EDGE,"E12.5.4"),sQuery(id+"F0.wireOp",EDGE,"E12.5.5"),sQuery(id+"F0.wireOp",EDGE,"E12.5.6"),sQuery(id+"F0.wireOp",EDGE,"E12.5.7"),sQuery(id+"F0.wireOp",EDGE,"E12.5.8"),sQuery(id+"F0.wireOp",EDGE,"E12.5.9"),sQuery(id+"F0.wireOp",EDGE,"E12.6.0"),sQuery(id+"F0.wireOp",EDGE,"E12.6.1"),sQuery(id+"F0.wireOp",EDGE,"E12.6.2"),sQuery(id+"F0.wireOp",EDGE,"E12.6.3"),sQuery(id+"F0.wireOp",EDGE,"E12.6.4"),sQuery(id+"F0.wireOp",EDGE,"E12.6.5"),sQuery(id+"F0.wireOp",EDGE,"E12.6.6"),sQuery(id+"F0.wireOp",EDGE,"E12.6.7"),sQuery(id+"F0.wireOp",EDGE,"E12.6.8"),sQuery(id+"F0.wireOp",EDGE,"E12.6.9"),sQuery(id+"F0.wireOp",EDGE,"E12.7.0"),sQuery(id+"F0.wireOp",EDGE,"E12.7.1"),sQuery(id+"F0.wireOp",EDGE,"E12.7.2"),sQuery(id+"F0.wireOp",EDGE,"E12.7.3"),sQuery(id+"F0.wireOp",EDGE,"E12.7.4"),sQuery(id+"F0.wireOp",EDGE,"E12.7.5"),sQuery(id+"F0.wireOp",EDGE,"E12.7.6"),sQuery(id+"F0.wireOp",EDGE,"E12.7.7"),sQuery(id+"F0.wireOp",EDGE,"E12.7.8"),sQuery(id+"F0.wireOp",EDGE,"E12.7.9"),sQuery(id+"F0.wireOp",EDGE,"E12.8.0"),sQuery(id+"F0.wireOp",EDGE,"E12.8.1"),sQuery(id+"F0.wireOp",EDGE,"E12.8.2"),sQuery(id+"F0.wireOp",EDGE,"E12.8.3"),sQuery(id+"F0.wireOp",EDGE,"E12.8.4"),sQuery(id+"F0.wireOp",EDGE,"E12.8.5"),sQuery(id+"F0.wireOp",EDGE,"E12.8.6"),sQuery(id+"F0.wireOp",EDGE,"E12.8.7"),sQuery(id+"F0.wireOp",EDGE,"E12.8.8"),sQuery(id+"F0.wireOp",EDGE,"E12.8.9"),sQuery(id+"F0.wireOp",EDGE,"E12.9.0"),sQuery(id+"F0.wireOp",EDGE,"E12.9.1"),sQuery(id+"F0.wireOp",EDGE,"E12.9.2"),sQuery(id+"F0.wireOp",EDGE,"E12.9.3"),sQuery(id+"F0.wireOp",EDGE,"E12.9.4"),sQuery(id+"F0.wireOp",EDGE,"E12.9.5"),sQuery(id+"F0.wireOp",EDGE,"E12.9.6"),sQuery(id+"F0.wireOp",EDGE,"E12.9.7"),sQuery(id+"F0.wireOp",EDGE,"E12.9.8"),sQuery(id+"F0.wireOp",EDGE,"E12.9.9"),sQuery(id+"F0.wireOp",EDGE,"E12.10.0"),sQuery(id+"F0.wireOp",EDGE,"E12.10.1"),sQuery(id+"F0.wireOp",EDGE,"E12.10.2"),sQuery(id+"F0.wireOp",EDGE,"E12.10.3"),sQuery(id+"F0.wireOp",EDGE,"E12.10.4"),sQuery(id+"F0.wireOp",EDGE,"E12.10.5"),sQuery(id+"F0.wireOp",EDGE,"E12.10.6"),sQuery(id+"F0.wireOp",EDGE,"E12.10.7"),sQuery(id+"F0.wireOp",EDGE,"E12.10.8"),sQuery(id+"F0.wireOp",EDGE,"E12.10.9"),sQuery(id+"F0.wireOp",EDGE,"E12.11.0"),sQuery(id+"F0.wireOp",EDGE,"E12.11.1"),sQuery(id+"F0.wireOp",EDGE,"E12.11.2"),sQuery(id+"F0.wireOp",EDGE,"E12.11.3"),sQuery(id+"F0.wireOp",EDGE,"E12.11.4"),sQuery(id+"F0.wireOp",EDGE,"E12.11.5"),sQuery(id+"F0.wireOp",EDGE,"E12.11.6"),sQuery(id+"F0.wireOp",EDGE,"E12.11.7"),sQuery(id+"F0.wireOp",EDGE,"E12.11.8"),sQuery(id+"F0.wireOp",EDGE,"E12.11.9"),sQuery(id+"F0.wireOp",EDGE,"E12.12.0"),sQuery(id+"F0.wireOp",EDGE,"E12.12.1"),sQuery(id+"F0.wireOp",EDGE,"E12.12.2"),sQuery(id+"F0.wireOp",EDGE,"E12.12.3"),sQuery(id+"F0.wireOp",EDGE,"E12.12.4"),sQuery(id+"F0.wireOp",EDGE,"E12.12.5"),sQuery(id+"F0.wireOp",EDGE,"E12.12.6"),sQuery(id+"F0.wireOp",EDGE,"E12.12.7"),sQuery(id+"F0.wireOp",EDGE,"E12.12.8"),sQuery(id+"F0.wireOp",EDGE,"E12.12.9"),sQuery(id+"F0.wireOp",EDGE,"E12.13.0"),sQuery(id+"F0.wireOp",EDGE,"E12.13.1"),sQuery(id+"F0.wireOp",EDGE,"E12.13.2"),sQuery(id+"F0.wireOp",EDGE,"E12.13.3"),sQuery(id+"F0.wireOp",EDGE,"E12.13.4"),sQuery(id+"F0.wireOp",EDGE,"E12.13.5"),sQuery(id+"F0.wireOp",EDGE,"E12.13.6"),sQuery(id+"F0.wireOp",EDGE,"E12.13.7"),sQuery(id+"F0.wireOp",EDGE,"E12.13.8"),sQuery(id+"F0.wireOp",EDGE,"E12.13.9"),sQuery(id+"F0.wireOp",EDGE,"E12.14.0"),sQuery(id+"F0.wireOp",EDGE,"E12.14.1"),sQuery(id+"F0.wireOp",EDGE,"E12.14.2"),sQuery(id+"F0.wireOp",EDGE,"E12.14.3"),sQuery(id+"F0.wireOp",EDGE,"E12.14.4"),sQuery(id+"F0.wireOp",EDGE,"E12.14.5"),sQuery(id+"F0.wireOp",EDGE,"E12.14.6"),sQuery(id+"F0.wireOp",EDGE,"E12.14.7"),sQuery(id+"F0.wireOp",EDGE,"E12.14.8"),sQuery(id+"F0.wireOp",EDGE,"E12.14.9"),sQuery(id+"F0.wireOp",EDGE,"E12.15.0"),sQuery(id+"F0.wireOp",EDGE,"E12.15.1"),sQuery(id+"F0.wireOp",EDGE,"E12.15.2"),sQuery(id+"F0.wireOp",EDGE,"E12.15.3"),sQuery(id+"F0.wireOp",EDGE,"E12.15.4"),sQuery(id+"F0.wireOp",EDGE,"E12.15.5"),sQuery(id+"F0.wireOp",EDGE,"E12.15.6"),sQuery(id+"F0.wireOp",EDGE,"E12.15.7"),sQuery(id+"F0.wireOp",EDGE,"E12.15.8"),sQuery(id+"F0.wireOp",EDGE,"E12.15.9"),sQuery(id+"F0.wireOp",EDGE,"E12.16.0"),sQuery(id+"F0.wireOp",EDGE,"E12.16.1"),sQuery(id+"F0.wireOp",EDGE,"E12.16.2"),sQuery(id+"F0.wireOp",EDGE,"E12.16.3"),sQuery(id+"F0.wireOp",EDGE,"E12.16.4"),sQuery(id+"F0.wireOp",EDGE,"E12.16.5"),sQuery(id+"F0.wireOp",EDGE,"E12.16.6"),sQuery(id+"F0.wireOp",EDGE,"E12.16.7"),sQuery(id+"F0.wireOp",EDGE,"E12.16.8"),sQuery(id+"F0.wireOp",EDGE,"E12.16.9"),sQuery(id+"F0.wireOp",EDGE,"E12.17.0"),sQuery(id+"F0.wireOp",EDGE,"E12.17.1"),sQuery(id+"F0.wireOp",EDGE,"E12.17.2"),sQuery(id+"F0.wireOp",EDGE,"E12.17.3"),sQuery(id+"F0.wireOp",EDGE,"E12.17.4"),sQuery(id+"F0.wireOp",EDGE,"E12.17.5"),sQuery(id+"F0.wireOp",EDGE,"E12.17.6"),sQuery(id+"F0.wireOp",EDGE,"E12.17.7"),sQuery(id+"F0.wireOp",EDGE,"E12.17.8"),sQuery(id+"F0.wireOp",EDGE,"E12.17.9"),sQuery(id+"F0.wireOp",EDGE,"E12.18.0"),sQuery(id+"F0.wireOp",EDGE,"E12.18.1"),sQuery(id+"F0.wireOp",EDGE,"E12.18.2"),sQuery(id+"F0.wireOp",EDGE,"E12.18.3"),sQuery(id+"F0.wireOp",EDGE,"E12.18.4"),sQuery(id+"F0.wireOp",EDGE,"E12.18.5"),sQuery(id+"F0.wireOp",EDGE,"E12.18.6"),sQuery(id+"F0.wireOp",EDGE,"E12.18.7"),sQuery(id+"F0.wireOp",EDGE,"E12.18.8"),sQuery(id+"F0.wireOp",EDGE,"E12.18.9"),sQuery(id+"F0.wireOp",EDGE,"E12.19.0"),sQuery(id+"F0.wireOp",EDGE,"E12.19.1"),sQuery(id+"F0.wireOp",EDGE,"E12.19.2"),sQuery(id+"F0.wireOp",EDGE,"E12.19.3"),sQuery(id+"F0.wireOp",EDGE,"E12.19.4"),sQuery(id+"F0.wireOp",EDGE,"E12.19.5"),sQuery(id+"F0.wireOp",EDGE,"E12.19.6"),sQuery(id+"F0.wireOp",EDGE,"E12.19.7"),sQuery(id+"F0.wireOp",EDGE,"E12.19.8"),sQuery(id+"F0.wireOp",EDGE,"E12.19.9"),sQuery(id+"F0.wireOp",EDGE,"E12.20.0"),sQuery(id+"F0.wireOp",EDGE,"E12.20.1"),sQuery(id+"F0.wireOp",EDGE,"E12.20.2"),sQuery(id+"F0.wireOp",EDGE,"E12.20.3"),sQuery(id+"F0.wireOp",EDGE,"E12.20.4"),sQuery(id+"F0.wireOp",EDGE,"E12.20.5"),sQuery(id+"F0.wireOp",EDGE,"E12.20.6"),sQuery(id+"F0.wireOp",EDGE,"E12.20.7"),sQuery(id+"F0.wireOp",EDGE,"E12.20.8"),sQuery(id+"F0.wireOp",EDGE,"E12.20.9"),sQuery(id+"F0.wireOp",EDGE,"E12.21.0"),sQuery(id+"F0.wireOp",EDGE,"E12.21.1"),sQuery(id+"F0.wireOp",EDGE,"E12.21.2"),sQuery(id+"F0.wireOp",EDGE,"E12.21.3"),sQuery(id+"F0.wireOp",EDGE,"E12.21.4"),sQuery(id+"F0.wireOp",EDGE,"E12.21.5"),sQuery(id+"F0.wireOp",EDGE,"E12.21.6"),sQuery(id+"F0.wireOp",EDGE,"E12.21.7"),sQuery(id+"F0.wireOp",EDGE,"E12.21.8"),sQuery(id+"F0.wireOp",EDGE,"E12.21.9"),sQuery(id+"F0.wireOp",EDGE,"E12.22.0"),sQuery(id+"F0.wireOp",EDGE,"E12.22.1"),sQuery(id+"F0.wireOp",EDGE,"E12.22.2"),sQuery(id+"F0.wireOp",EDGE,"E12.22.3"),sQuery(id+"F0.wireOp",EDGE,"E12.22.4"),sQuery(id+"F0.wireOp",EDGE,"E12.22.5"),sQuery(id+"F0.wireOp",EDGE,"E12.22.6"),sQuery(id+"F0.wireOp",EDGE,"E12.22.7"),sQuery(id+"F0.wireOp",EDGE,"E12.22.8"),sQuery(id+"F0.wireOp",EDGE,"E12.22.9"),sQuery(id+"F0.wireOp",EDGE,"E12.23.0"),sQuery(id+"F0.wireOp",EDGE,"E12.23.1"),sQuery(id+"F0.wireOp",EDGE,"E12.23.2"),sQuery(id+"F0.wireOp",EDGE,"E12.23.3"),sQuery(id+"F0.wireOp",EDGE,"E12.23.4"),sQuery(id+"F0.wireOp",EDGE,"E12.23.5"),sQuery(id+"F0.wireOp",EDGE,"E12.23.6"),sQuery(id+"F0.wireOp",EDGE,"E12.23.7"),sQuery(id+"F0.wireOp",EDGE,"E12.23.8"),sQuery(id+"F0.wireOp",EDGE,"E12.23.9")])],"isStart":false});
            var sketch = newSketch(context, id + "F2", { "sketchPlane" : qUnion([Q0])});
            skCircle(sketch, "E13", {"center": v(0, 0) * mm, "radius": 5.08 * mm});
            skSolve(sketch);
        }
        {
            var Q0;
            Q0 = qSketchRegion(id + "F2", true);
            extrude(context, id + "F3", {"entities" : qUnion([Q0]), "operationType" : NewBodyOperationType.REMOVE, "endBound" : BoundingType.THROUGH_ALL, "oppositeDirection" : true, "depth" : 25.4 * mm});
        }
    });
